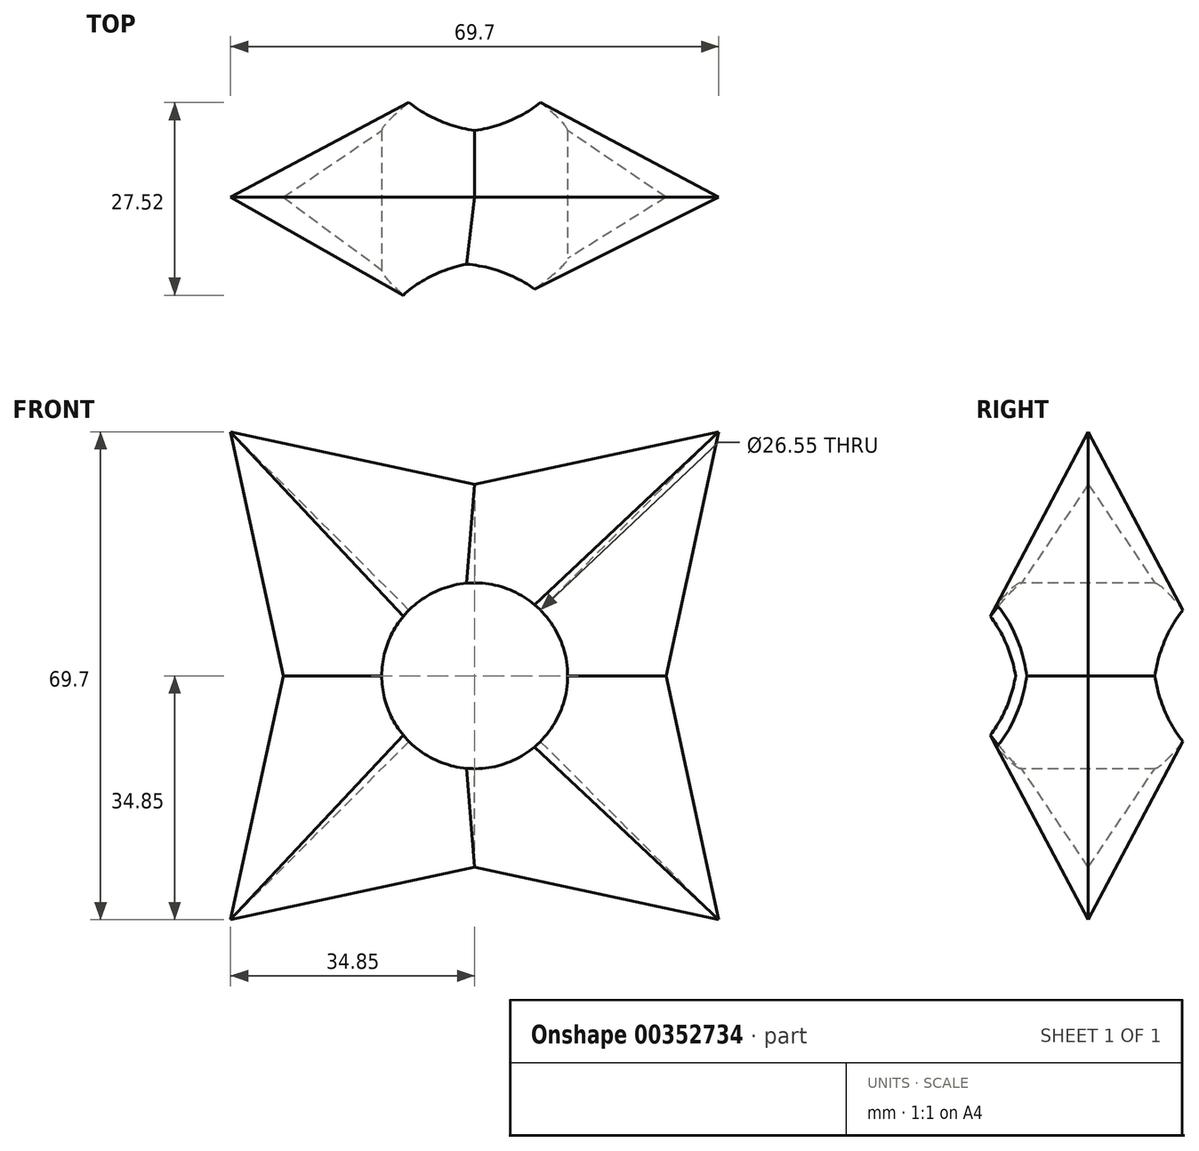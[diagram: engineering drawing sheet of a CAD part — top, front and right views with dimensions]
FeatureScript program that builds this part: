
annotation { "Feature Type Name" : "Feature", "Feature Type Description" : "" }
export const myFeature = defineFeature(function(context is Context, id is Id, definition is map)
    precondition{}
    {
        {
            var Q0;
            Q0=qCreatedBy(makeId("Front.planeOp"),FACE);
            var sketch = newSketch(context, id + "F0", { "sketchPlane" : qUnion([Q0])});
            skPoint(sketch, "E0.0.midPoint", {"position": v(0, 34.85) * mm});
            skLineSegment(sketch, "E1", {"start": v(-34.85, -34.85) * mm, "end": v(-27.33, 0) * mm});
            skLineSegment(sketch, "E2", {"start": v(-34.85, 34.85) * mm, "end": v(-27.33, 0) * mm});
            skLineSegment(sketch, "E3", {"start": v(-34.85, 34.85) * mm, "end": v(0, 27.33) * mm});
            skLineSegment(sketch, "E4", {"start": v(0, 27.33) * mm, "end": v(34.85, 34.85) * mm});
            skLineSegment(sketch, "E5", {"start": v(34.85, 34.85) * mm, "end": v(27.33, 0) * mm});
            skLineSegment(sketch, "E6", {"start": v(27.33, 0) * mm, "end": v(34.85, -34.85) * mm});
            skLineSegment(sketch, "E7", {"start": v(-34.85, -34.85) * mm, "end": v(0, -27.33) * mm});
            skLineSegment(sketch, "E8", {"start": v(0, -27.33) * mm, "end": v(34.85, -34.85) * mm});
            skPoint(sketch, "E9.end.orphan", {"position": v(0, -34.85) * mm});
            skPoint(sketch, "E0.cCircle.center.orphan", {"position": v(0, 0) * mm});
            skSolve(sketch);
        }
        {
            var Q0;
            Q0=qCreatedBy(makeId("Front.planeOp"),FACE);
            var Q1;
            Q1 = qBodyType(qCreatedBy(id + "F2" ,EDGE), BodyType.WIRE);
            cPlane(context, id + "F1", {"entities" : qUnion([Q0, Q1]), "cplaneType" : CPlaneType.OFFSET, "offset" : 18.5 * mm, "width" : 150 * mm, "height" : 150 * mm});
        }
        {
            var Q0;
            Q0=qCreatedBy(id+"F1.planeOp",FACE);
            var sketch = newSketch(context, id + "F2", { "sketchPlane" : qUnion([Q0])});
            skCircle(sketch, "E10", {"center": v(-2.29, 0) * mm, "radius": 1.15 * mm});
            skSolve(sketch);
        }
        {
            var Q0;
            Q0=makeQuery(id+"F0.imprint","IMPRINT",FACE,{"disambiguationData":[TD([[makeQuery(id+"F0.imprint","IMPRINT",EDGE,{"derivedFrom":sQuery(id+"F0.wireOp",EDGE,"E1")}),-1.0]])]});
            var Q1;
            Q1=sQuery(id+"F2.wireOp",VERTEX,"E10.center");
            loft(context, id + "F3", {"sheetProfilesArray" : [{ "sheetProfileEntities" : qUnion([Q0]) }, { "sheetProfileEntities" : qUnion([Q1]) }]});
        }
        {
            var Q0;
            Q0=qCreatedBy(makeId("Front.planeOp"),FACE);
            cPlane(context, id + "F4", {"entities" : qUnion([Q0]), "cplaneType" : CPlaneType.OFFSET, "offset" : 18.5 * mm, "oppositeDirection" : true, "width" : 150 * mm, "height" : 150 * mm});
        }
        {
            var Q0;
            Q0=qCreatedBy(id+"F4.planeOp",FACE);
            var sketch = newSketch(context, id + "F5", { "sketchPlane" : qUnion([Q0])});
            skCircle(sketch, "E11", {"center": v(0, 0) * mm, "radius": 1.1 * mm});
            skSolve(sketch);
        }
        {
            var Q1;
            Q1=makeQuery(id+"F3.opLoft","CAP_FACE",FACE,{"disambiguationData":[OSD([makeQuery(id+"F0.imprint","IMPRINT",FACE,{"disambiguationData":[TD([[makeQuery(id+"F0.imprint","IMPRINT",EDGE,{"derivedFrom":sQuery(id+"F0.wireOp",EDGE,"E1")}),-1.0]])]})])],"isStart":true});
            var Q2;
            Q2=sQuery(id+"F5.wireOp",VERTEX,"E11.center");
            loft(context, id + "F6", {"operationType" : NewBodyOperationType.ADD, "sheetProfilesArray" : [{ "sheetProfileEntities" : qUnion([Q1]) }, { "sheetProfileEntities" : qUnion([Q2]) }]});
        }
        {
            var Q0;
            Q0=qCreatedBy(makeId("Front.planeOp"),FACE);
            var sketch = newSketch(context, id + "F7", { "sketchPlane" : qUnion([Q0])});
            skCircle(sketch, "E12", {"center": v(0, 0) * mm, "radius": 13.27 * mm});
            skSolve(sketch);
        }
        {
            var Q0;
            Q0 = qSketchRegion(id + "F7", true);
            var Q1;
            Q1=sQuery(id+"F7.wireOp",EDGE,"E12");
            extrude(context, id + "F8", {"entities" : qUnion([Q0]), "operationType" : NewBodyOperationType.REMOVE, "surfaceEntities" : qUnion([Q1]), "endBound" : BoundingType.SYMMETRIC, "oppositeDirection" : true, "depth" : 58.4 * mm});
        }
    });
